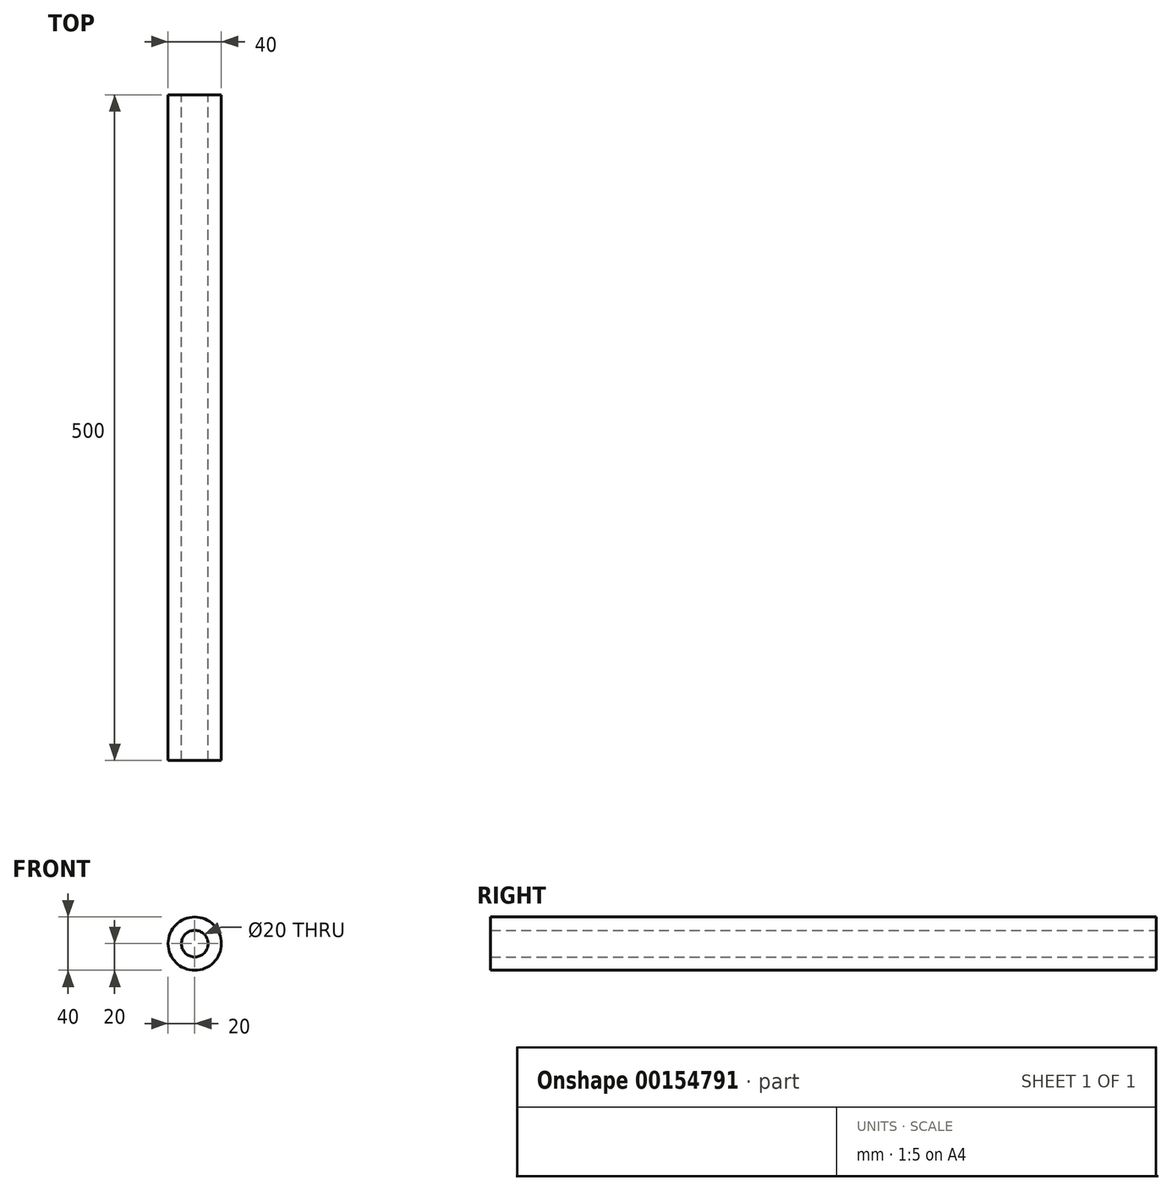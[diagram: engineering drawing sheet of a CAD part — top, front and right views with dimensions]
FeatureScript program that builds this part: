
annotation { "Feature Type Name" : "Feature", "Feature Type Description" : "" }
export const myFeature = defineFeature(function(context is Context, id is Id, definition is map)
    precondition{}
    {
        {
            var Q0;
            Q0=qCreatedBy(makeId("Front.planeOp"),FACE);
            var sketch = newSketch(context, id + "F0", { "sketchPlane" : qUnion([Q0])});
            skCircle(sketch, "E0", {"center": v(0, 0) * mm, "radius": 20 * mm});
            skCircle(sketch, "E1", {"center": v(0, 0) * mm, "radius": 10 * mm});
            skSolve(sketch);
        }
        {
            var Q0;
            Q0 = qSketchRegion(id + "F0", true);
            extrude(context, id + "F1", {"entities" : qUnion([Q0]), "depth" : 500 * mm});
        }
    });
